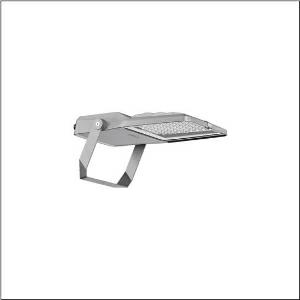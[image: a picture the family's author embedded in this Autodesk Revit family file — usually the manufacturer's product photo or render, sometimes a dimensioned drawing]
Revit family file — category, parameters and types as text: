
# Revit family: floodlight_fl_21_iq_mini___pl64_5xa7772d1e1a_af72
name_source: partatom
category: Lighting Fixtures
units: mm (PartAtom-declared; Revit-internal decimal feet)

## family parameters
Cut with Voids When Loaded = No
Host = Face
Light Source = No
Part Type = Normal
Room Calculation Point = No
Round Connector Dimension = Use Diameter
Shared = No

## types (1)
- --- (1 x LED, 14250 lm, 143 W, 2200K)
    Apparent Load = 143 VA
    CIE Flux Codes = 28 80 98 100 100
    Color Rendering = 70
    Color Temperature = 2200K
    Default Elevation = 1800 mm
    Description = Floodlight FL 21 iQ mini, floodlight, primary light control with lens, of PMMA, primary optical cover: protective disc, of toughened safety glass, transparent, light distribution: PL64, light emission: direct distribution, installation type: surface-mounted, LED, High Power LED, rated luminous flux: 14.250lm, luminous efficacy: 100lm/W, light colour: 722, colour temperature: 2200K, control gear: iQ Street-Remote/DALI, control: Street-Remote, Auto-Match, Temp-Guard, Night-Set, Smart-Wire, Desk-Remote (wireless, voltage-free reading and setting of iQ features in the workshop via application-optimized NFC function/RFID function), optimised constant luminous flux control (CLO 2.0), with terminal, 6-pole, mains connection: 220..240V, AC, 50/60Hz, start of lifetime: 143W, end of service life: 152W, reduction: 61W, luminaire housing, of diecast aluminium, powder-coated, Siteco® metallic grey (DB 702S), corrosivity category C5 mid according to DIN EN ISO 12944, suitable for swimming pools, chlorine-resistant, sealing non-destructively replaceable, mounting bracket, of steel, galvanised, powder-coated, Siteco® metallic grey (DB 702S), protection rating (complete): IP66, insulation class (complete): insulation class II (safety insulation), certification: CE, ENEC, VDE, protection symbol: D, impact resistance: IK08, permissible operating ambient temperature: -40..+40°C, permissible operating ambient temperature for outdoor applications: -40..+50°C, standard: DIN EN 12944, LABS conformity tested according to VDMA 24364:2018-05, packaging unit: 1 piece

Light Distribution: PL64
    Height = 70 mm
    Lamp = 1 x LED
    Lamp Light Flux = 14250 lm
    Lamp Power = 143 W
    Lamp count = 1
    Length = 485 mm
    Luminous efficacy = 100 lm/W
    Manufacturer = Siteco
    ModVariant = No
    Model = 5XA7772D1E1A
    Number of Poles = 1
    OnlyDefault = Yes
    Power Factor = 1
    Product Name = Floodlight FL 21 iQ mini | PL64
    Product group = floodlight | pylon annexe
    ProductGroupID = 6200
    Protection Class = Protection class II
    Protection Degree = IP 66
    RLX_Detail_Level = 1
    RLX_Emergency_Light_Flux = 0 lm
    RLX_Emergency_Type = 0
    RLX_Emergency_Type_DB = No
    RlxData = <blob elided: 96541 chars, md5=a1271228>
    Socket = socket
    Standby Power = 0 W
    System Light Flux = 14250 lm
    System Power = 143 W
    Type Comments = factory setting: luminous flux: 100 % | dim-lin: 254 | 730 mA
    Type Image = l_1006845.jpg
    URL = http://relux.com
    VarID = @adj_165916
    Voltage = 0 V
    Weight = 0.00 kg
    Width = 337 mm

## geometry (parser evidence)
native form markers: Blend x4, Sweep x11
no freeform markers — native parametric forms only
